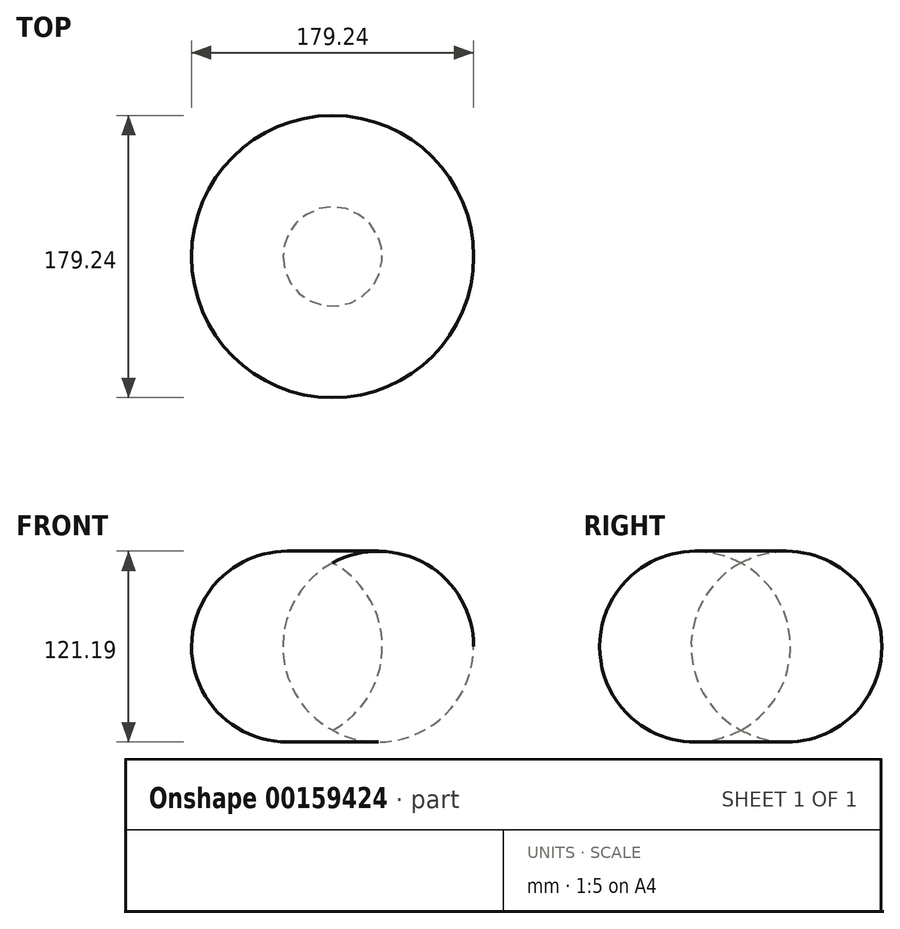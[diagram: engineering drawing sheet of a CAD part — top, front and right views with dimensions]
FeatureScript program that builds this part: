
annotation { "Feature Type Name" : "Feature", "Feature Type Description" : "" }
export const myFeature = defineFeature(function(context is Context, id is Id, definition is map)
    precondition{}
    {
        {
            var Q0;
            Q0=qCreatedBy(makeId("Front.planeOp"),FACE);
            var sketch = newSketch(context, id + "F0", { "sketchPlane" : qUnion([Q0])});
            skLineSegment(sketch, "E0", {"start": v(0, 52.3) * mm, "end": v(0, -54.08) * mm});
            skArc(sketch, "E1", {"start": v(0, -54.08) * mm, "mid": v(31.57, -0.9) * mm, "end": v(0, 52.3) * mm});
            skSolve(sketch);
        }
        {
            var Q0;
            Q0=makeQuery(id+"F0.imprint","IMPRINT",FACE,{"disambiguationData":[TD([[makeQuery(id+"F0.imprint","IMPRINT",EDGE,{"derivedFrom":sQuery(id+"F0.wireOp",EDGE,"E0")}),1.0]])]});
            var Q1;
            Q1=sQuery(id+"F0.wireOp",EDGE,"E0");
            revolve(context, id + "F1", {"entities" : qUnion([Q0]), "axis" : qUnion([Q1]), "revolveType" : RevolveType.FULL});
        }
    });
